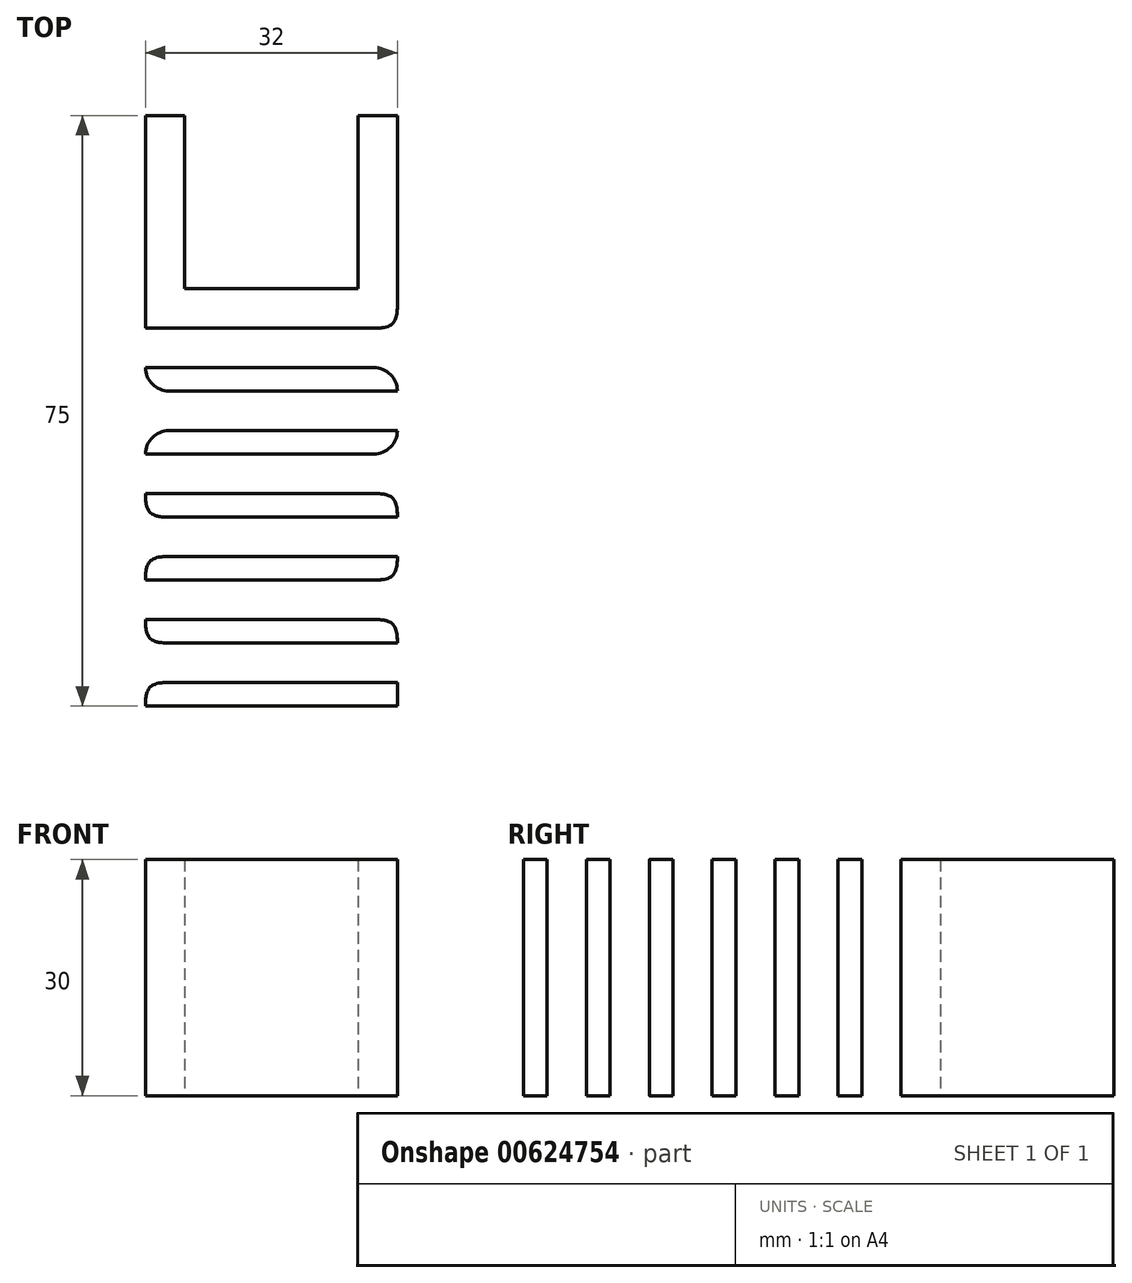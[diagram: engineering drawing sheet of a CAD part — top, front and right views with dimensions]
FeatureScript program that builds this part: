
annotation { "Feature Type Name" : "Feature", "Feature Type Description" : "" }
export const myFeature = defineFeature(function(context is Context, id is Id, definition is map)
    precondition{}
    {
        {
            var Q0;
            Q0=qCreatedBy(makeId("Top.planeOp"),FACE);
            var sketch = newSketch(context, id + "F0", { "sketchPlane" : qUnion([Q0])});
            skLineSegment(sketch, "E0.bottom", {"start": v(-14.17, -5.75) * mm, "end": v(7.83, -5.75) * mm});
            skLineSegment(sketch, "E0.top", {"start": v(-14.17, -27.75) * mm, "end": v(7.83, -27.75) * mm});
            skLineSegment(sketch, "E0.left", {"start": v(-14.17, -5.75) * mm, "end": v(-14.17, -27.75) * mm});
            skLineSegment(sketch, "E0.right", {"start": v(7.83, -5.75) * mm, "end": v(7.83, -27.75) * mm});
            skLineSegment(sketch, "E1.bottom", {"start": v(-14.17, -5.75) * mm, "end": v(-19.17, -5.75) * mm});
            skLineSegment(sketch, "E1.top", {"start": v(-14.17, -27.75) * mm, "end": v(-19.17, -27.75) * mm});
            skLineSegment(sketch, "E1.right", {"start": v(-19.17, -5.75) * mm, "end": v(-19.17, -27.75) * mm});
            skLineSegment(sketch, "E2.bottom", {"start": v(7.83, -5.75) * mm, "end": v(12.83, -5.75) * mm});
            skLineSegment(sketch, "E2.top", {"start": v(7.83, -27.75) * mm, "end": v(12.83, -27.75) * mm});
            skLineSegment(sketch, "E2.right", {"start": v(12.83, -5.75) * mm, "end": v(12.83, -27.75) * mm});
            skLineSegment(sketch, "E3.bottom", {"start": v(-19.17, -27.75) * mm, "end": v(12.83, -27.75) * mm});
            skLineSegment(sketch, "E3.top", {"start": v(-19.17, -32.75) * mm, "end": v(12.83, -32.75) * mm});
            skLineSegment(sketch, "E3.left", {"start": v(-19.17, -27.75) * mm, "end": v(-19.17, -32.75) * mm});
            skLineSegment(sketch, "E3.right", {"start": v(12.83, -27.75) * mm, "end": v(12.83, -32.75) * mm});
            skLineSegment(sketch, "E4.bottom", {"start": v(-19.17, -32.75) * mm, "end": v(-16.17, -32.75) * mm});
            skLineSegment(sketch, "E4.top", {"start": v(-19.17, -37.75) * mm, "end": v(-16.17, -37.75) * mm});
            skLineSegment(sketch, "E4.left", {"start": v(-19.17, -32.75) * mm, "end": v(-19.17, -37.75) * mm});
            skLineSegment(sketch, "E4.right", {"start": v(-16.17, -32.75) * mm, "end": v(-16.17, -37.75) * mm});
            skLineSegment(sketch, "E5.bottom", {"start": v(-19.17, -37.75) * mm, "end": v(9.83, -37.75) * mm});
            skLineSegment(sketch, "E5.top", {"start": v(-16.17, -40.75) * mm, "end": v(12.83, -40.75) * mm});
            skLineSegment(sketch, "E5.left", {"start": v(-19.17, -37.75) * mm, "end": v(-19.17, -37.75) * mm});
            skLineSegment(sketch, "E5.right", {"start": v(12.83, -40.75) * mm, "end": v(12.83, -40.75) * mm});
            skLineSegment(sketch, "E6.bottom", {"start": v(12.83, -40.75) * mm, "end": v(9.83, -40.75) * mm});
            skLineSegment(sketch, "E6.top", {"start": v(12.83, -45.75) * mm, "end": v(9.83, -45.75) * mm});
            skLineSegment(sketch, "E6.left", {"start": v(12.83, -40.75) * mm, "end": v(12.83, -45.75) * mm});
            skLineSegment(sketch, "E6.right", {"start": v(9.83, -40.75) * mm, "end": v(9.83, -45.75) * mm});
            skLineSegment(sketch, "E7.bottom", {"start": v(12.83, -45.75) * mm, "end": v(-16.17, -45.75) * mm});
            skLineSegment(sketch, "E7.top", {"start": v(9.83, -48.75) * mm, "end": v(-19.17, -48.75) * mm});
            skLineSegment(sketch, "E7.left", {"start": v(12.83, -45.75) * mm, "end": v(12.83, -45.75) * mm});
            skLineSegment(sketch, "E7.right", {"start": v(-19.17, -48.75) * mm, "end": v(-19.17, -48.75) * mm});
            skLineSegment(sketch, "E8.bottom", {"start": v(-19.17, -48.75) * mm, "end": v(-16.17, -48.75) * mm});
            skLineSegment(sketch, "E8.top", {"start": v(-19.17, -53.75) * mm, "end": v(-16.17, -53.75) * mm});
            skLineSegment(sketch, "E8.left", {"start": v(-19.17, -48.75) * mm, "end": v(-19.17, -53.75) * mm});
            skLineSegment(sketch, "E8.right", {"start": v(-16.17, -48.75) * mm, "end": v(-16.17, -53.75) * mm});
            skLineSegment(sketch, "E9.bottom", {"start": v(-19.17, -53.75) * mm, "end": v(12.83, -53.75) * mm});
            skLineSegment(sketch, "E9.top", {"start": v(-19.17, -56.75) * mm, "end": v(12.83, -56.75) * mm});
            skLineSegment(sketch, "E9.left", {"start": v(-19.17, -53.75) * mm, "end": v(-19.17, -56.75) * mm});
            skLineSegment(sketch, "E9.right", {"start": v(12.83, -53.75) * mm, "end": v(12.83, -56.75) * mm});
            skPoint(sketch, "E10.visualSharp", {"position": v(12.83, -37.75) * mm});
            skArc(sketch, "E10.filletArc", {"start": v(12.83, -40.75) * mm, "mid": v(11.96, -38.63) * mm, "end": v(9.83, -37.75) * mm});
            skPoint(sketch, "E11.visualSharp", {"position": v(12.83, -48.75) * mm});
            skArc(sketch, "E11.filletArc", {"start": v(9.83, -48.75) * mm, "mid": v(11.96, -47.87) * mm, "end": v(12.83, -45.75) * mm});
            skPoint(sketch, "E12.visualSharp", {"position": v(-19.17, -45.75) * mm});
            skArc(sketch, "E12.filletArc", {"start": v(-16.17, -45.75) * mm, "mid": v(-18.29, -46.63) * mm, "end": v(-19.17, -48.75) * mm});
            skPoint(sketch, "E13.visualSharp", {"position": v(-19.17, -40.75) * mm});
            skArc(sketch, "E13.filletArc", {"start": v(-19.17, -37.75) * mm, "mid": v(-18.29, -39.87) * mm, "end": v(-16.17, -40.75) * mm});
            skLineSegment(sketch, "E14.bottom", {"start": v(12.83, -56.75) * mm, "end": v(9.98, -56.75) * mm});
            skLineSegment(sketch, "E14.top", {"start": v(12.83, -61.75) * mm, "end": v(9.98, -61.75) * mm});
            skLineSegment(sketch, "E14.left", {"start": v(12.83, -56.75) * mm, "end": v(12.83, -61.75) * mm});
            skLineSegment(sketch, "E14.right", {"start": v(9.98, -56.75) * mm, "end": v(9.98, -61.75) * mm});
            skLineSegment(sketch, "E15.bottom", {"start": v(12.83, -61.75) * mm, "end": v(-19.17, -61.75) * mm});
            skLineSegment(sketch, "E15.top", {"start": v(12.83, -64.75) * mm, "end": v(-19.17, -64.75) * mm});
            skLineSegment(sketch, "E15.left", {"start": v(12.83, -61.75) * mm, "end": v(12.83, -64.75) * mm});
            skLineSegment(sketch, "E15.right", {"start": v(-19.17, -61.75) * mm, "end": v(-19.17, -64.75) * mm});
            skLineSegment(sketch, "E16.bottom", {"start": v(-19.17, -64.75) * mm, "end": v(-16.17, -64.75) * mm});
            skLineSegment(sketch, "E16.top", {"start": v(-19.17, -69.75) * mm, "end": v(-16.17, -69.75) * mm});
            skLineSegment(sketch, "E16.left", {"start": v(-19.17, -64.75) * mm, "end": v(-19.17, -69.75) * mm});
            skLineSegment(sketch, "E16.right", {"start": v(-16.17, -64.75) * mm, "end": v(-16.17, -69.75) * mm});
            skLineSegment(sketch, "E17.bottom", {"start": v(-19.17, -69.75) * mm, "end": v(12.83, -69.75) * mm});
            skLineSegment(sketch, "E17.top", {"start": v(-19.17, -72.75) * mm, "end": v(12.83, -72.75) * mm});
            skLineSegment(sketch, "E17.left", {"start": v(-19.17, -69.75) * mm, "end": v(-19.17, -72.75) * mm});
            skLineSegment(sketch, "E17.right", {"start": v(12.83, -69.75) * mm, "end": v(12.83, -72.75) * mm});
            skLineSegment(sketch, "E18.bottom", {"start": v(12.83, -72.75) * mm, "end": v(9.98, -72.75) * mm});
            skLineSegment(sketch, "E18.top", {"start": v(12.83, -77.75) * mm, "end": v(9.98, -77.75) * mm});
            skLineSegment(sketch, "E18.left", {"start": v(12.83, -72.75) * mm, "end": v(12.83, -77.75) * mm});
            skLineSegment(sketch, "E18.right", {"start": v(9.98, -72.75) * mm, "end": v(9.98, -77.75) * mm});
            skLineSegment(sketch, "E19.bottom", {"start": v(12.83, -77.75) * mm, "end": v(-19.17, -77.75) * mm});
            skLineSegment(sketch, "E19.top", {"start": v(12.83, -80.75) * mm, "end": v(-19.17, -80.75) * mm});
            skLineSegment(sketch, "E19.left", {"start": v(12.83, -77.75) * mm, "end": v(12.83, -80.75) * mm});
            skLineSegment(sketch, "E19.right", {"start": v(-19.17, -77.75) * mm, "end": v(-19.17, -80.75) * mm});
            skSolve(sketch);
        }
        {
            var Q0;
            Q0=makeQuery(id+"F0.imprint","IMPRINT",FACE,{"disambiguationData":[TD([[makeQuery(id+"F0.imprint","IMPRINT",EDGE,{"derivedFrom":sQuery(id+"F0.wireOp",EDGE,"E1.bottom")}),1.0]])]});
            var Q1;
            Q1=makeQuery(id+"F0.imprint","IMPRINT",FACE,{"disambiguationData":[TD([[makeQuery(id+"F0.imprint","IMPRINT",EDGE,{"derivedFrom":sQuery(id+"F0.wireOp",EDGE,"E3.top")}),1.0]])]});
            var Q2;
            Q2=makeQuery(id+"F0.imprint","IMPRINT",FACE,{"disambiguationData":[TD([[makeQuery(id+"F0.imprint","IMPRINT",EDGE,{"derivedFrom":sQuery(id+"F0.wireOp",EDGE,"E2.bottom")}),-1.0]])]});
            var Q3;
            Q3=makeQuery(id+"F0.imprint","IMPRINT",FACE,{"disambiguationData":[TD([[makeQuery(id+"F0.imprint","IMPRINT",EDGE,{"derivedFrom":sQuery(id+"F0.wireOp",EDGE,"E4.bottom")}),-1.0]])]});
            var Q4;
            Q4=makeQuery(id+"F0.imprint","IMPRINT",FACE,{"disambiguationData":[TD([[makeQuery(id+"F0.imprint","IMPRINT",EDGE,{"derivedFrom":sQuery(id+"F0.wireOp",EDGE,"E5.top")}),1.0]])]});
            var Q5;
            Q5=makeQuery(id+"F0.imprint","IMPRINT",FACE,{"disambiguationData":[TD([[makeQuery(id+"F0.imprint","IMPRINT",EDGE,{"derivedFrom":sQuery(id+"F0.wireOp",EDGE,"E6.bottom")}),1.0]])]});
            var Q6;
            Q6=makeQuery(id+"F0.imprint","IMPRINT",FACE,{"disambiguationData":[TD([[makeQuery(id+"F0.imprint","IMPRINT",EDGE,{"derivedFrom":sQuery(id+"F0.wireOp",EDGE,"E7.top")}),-1.0]])]});
            var Q7;
            Q7=makeQuery(id+"F0.imprint","IMPRINT",FACE,{"disambiguationData":[TD([[makeQuery(id+"F0.imprint","IMPRINT",EDGE,{"derivedFrom":sQuery(id+"F0.wireOp",EDGE,"E8.bottom")}),-1.0]])]});
            var Q8;
            Q8=makeQuery(id+"F0.imprint","IMPRINT",FACE,{"disambiguationData":[TD([[makeQuery(id+"F0.imprint","IMPRINT",EDGE,{"derivedFrom":sQuery(id+"F0.wireOp",EDGE,"E9.top")}),1.0]])]});
            var Q9;
            Q9=makeQuery(id+"F0.imprint","IMPRINT",FACE,{"disambiguationData":[TD([[makeQuery(id+"F0.imprint","IMPRINT",EDGE,{"derivedFrom":sQuery(id+"F0.wireOp",EDGE,"E14.bottom")}),1.0]])]});
            var Q10;
            Q10=makeQuery(id+"F0.imprint","IMPRINT",FACE,{"disambiguationData":[TD([[makeQuery(id+"F0.imprint","IMPRINT",EDGE,{"derivedFrom":sQuery(id+"F0.wireOp",EDGE,"E15.top")}),-1.0]])]});
            var Q11;
            Q11=makeQuery(id+"F0.imprint","IMPRINT",FACE,{"disambiguationData":[TD([[makeQuery(id+"F0.imprint","IMPRINT",EDGE,{"derivedFrom":sQuery(id+"F0.wireOp",EDGE,"E16.bottom")}),-1.0]])]});
            var Q12;
            Q12=makeQuery(id+"F0.imprint","IMPRINT",FACE,{"disambiguationData":[TD([[makeQuery(id+"F0.imprint","IMPRINT",EDGE,{"derivedFrom":sQuery(id+"F0.wireOp",EDGE,"E17.top")}),1.0]])]});
            var Q13;
            Q13=makeQuery(id+"F0.imprint","IMPRINT",FACE,{"disambiguationData":[TD([[makeQuery(id+"F0.imprint","IMPRINT",EDGE,{"derivedFrom":sQuery(id+"F0.wireOp",EDGE,"E18.bottom")}),1.0]])]});
            var Q14;
            Q14=makeQuery(id+"F0.imprint","IMPRINT",FACE,{"disambiguationData":[TD([[makeQuery(id+"F0.imprint","IMPRINT",EDGE,{"derivedFrom":sQuery(id+"F0.wireOp",EDGE,"E19.top")}),-1.0]])]});
            extrude(context, id + "F1", {"entities" : qUnion([Q0, Q1, Q2, Q3, Q4, Q5, Q6, Q7, Q8, Q9, Q10, Q11, Q12, Q13, Q14]), "depth" : 30 * mm, "offsetDistance" : 25 * mm});
        }
        {
            var Q0;
            Q0=makeQuery(id+"F1.opExtrude","SWEPT_EDGE",EDGE,{"disambiguationData":[OSD([sQuery(id+"F0.wireOp",EDGE,"E4.right"),sQuery(id+"F0.wireOp",EDGE,"E5.bottom")])]});
            var Q1;
            Q1=makeQuery(id+"F1.opExtrude","SWEPT_EDGE",EDGE,{"disambiguationData":[OSD([sQuery(id+"F0.wireOp",EDGE,"E3.top"),sQuery(id+"F0.wireOp",EDGE,"E4.bottom"),sQuery(id+"F0.wireOp",EDGE,"E4.right")])]});
            var Q2;
            Q2=makeQuery(id+"F1.opExtrude","SWEPT_EDGE",EDGE,{"disambiguationData":[OSD([sQuery(id+"F0.wireOp",EDGE,"E5.top"),sQuery(id+"F0.wireOp",EDGE,"E6.bottom"),sQuery(id+"F0.wireOp",EDGE,"E6.right")])]});
            var Q3;
            Q3=makeQuery(id+"F1.opExtrude","SWEPT_EDGE",EDGE,{"disambiguationData":[OSD([sQuery(id+"F0.wireOp",EDGE,"E6.right"),sQuery(id+"F0.wireOp",EDGE,"E7.bottom")])]});
            var Q4;
            Q4=makeQuery(id+"F1.opExtrude","SWEPT_EDGE",EDGE,{"disambiguationData":[OSD([sQuery(id+"F0.wireOp",EDGE,"E7.top"),sQuery(id+"F0.wireOp",EDGE,"E8.bottom"),sQuery(id+"F0.wireOp",EDGE,"E8.right")])]});
            var Q5;
            Q5=makeQuery(id+"F1.opExtrude","SWEPT_EDGE",EDGE,{"disambiguationData":[OSD([sQuery(id+"F0.wireOp",EDGE,"E8.right"),sQuery(id+"F0.wireOp",EDGE,"E9.bottom")])]});
            var Q6;
            Q6=makeQuery(id+"F1.opExtrude","SWEPT_EDGE",EDGE,{"disambiguationData":[OSD([sQuery(id+"F0.wireOp",EDGE,"E9.bottom"),sQuery(id+"F0.wireOp",EDGE,"E9.right")])]});
            var Q7;
            Q7=makeQuery(id+"F1.opExtrude","SWEPT_EDGE",EDGE,{"disambiguationData":[OSD([sQuery(id+"F0.wireOp",EDGE,"E15.top"),sQuery(id+"F0.wireOp",EDGE,"E15.left")])]});
            var Q8;
            Q8=makeQuery(id+"F1.opExtrude","SWEPT_EDGE",EDGE,{"disambiguationData":[OSD([sQuery(id+"F0.wireOp",EDGE,"E17.bottom"),sQuery(id+"F0.wireOp",EDGE,"E17.right")])]});
            var Q9;
            Q9=makeQuery(id+"F1.opExtrude","SWEPT_EDGE",EDGE,{"disambiguationData":[OSD([sQuery(id+"F0.wireOp",EDGE,"E17.top"),sQuery(id+"F0.wireOp",EDGE,"E18.bottom"),sQuery(id+"F0.wireOp",EDGE,"E18.right")])]});
            var Q10;
            Q10=makeQuery(id+"F1.opExtrude","SWEPT_EDGE",EDGE,{"disambiguationData":[OSD([sQuery(id+"F0.wireOp",EDGE,"E18.right"),sQuery(id+"F0.wireOp",EDGE,"E19.bottom")])]});
            var Q11;
            Q11=makeQuery(id+"F1.opExtrude","SWEPT_EDGE",EDGE,{"disambiguationData":[OSD([sQuery(id+"F0.wireOp",EDGE,"E17.top"),sQuery(id+"F0.wireOp",EDGE,"E17.left")])]});
            var Q12;
            Q12=makeQuery(id+"F1.opExtrude","SWEPT_EDGE",EDGE,{"disambiguationData":[OSD([sQuery(id+"F0.wireOp",EDGE,"E15.bottom"),sQuery(id+"F0.wireOp",EDGE,"E15.right")])]});
            var Q13;
            Q13=makeQuery(id+"F1.opExtrude","SWEPT_EDGE",EDGE,{"disambiguationData":[OSD([sQuery(id+"F0.wireOp",EDGE,"E9.top"),sQuery(id+"F0.wireOp",EDGE,"E14.bottom"),sQuery(id+"F0.wireOp",EDGE,"E14.right")])]});
            var Q14;
            Q14=makeQuery(id+"F1.opExtrude","SWEPT_EDGE",EDGE,{"disambiguationData":[OSD([sQuery(id+"F0.wireOp",EDGE,"E14.right"),sQuery(id+"F0.wireOp",EDGE,"E15.bottom")])]});
            var Q15;
            Q15=makeQuery(id+"F1.opExtrude","SWEPT_EDGE",EDGE,{"disambiguationData":[OSD([sQuery(id+"F0.wireOp",EDGE,"E9.top"),sQuery(id+"F0.wireOp",EDGE,"E9.left")])]});
            var Q16;
            Q16=makeQuery(id+"F1.opExtrude","SWEPT_EDGE",EDGE,{"disambiguationData":[OSD([sQuery(id+"F0.wireOp",EDGE,"E15.top"),sQuery(id+"F0.wireOp",EDGE,"E16.bottom"),sQuery(id+"F0.wireOp",EDGE,"E16.right")])]});
            var Q17;
            Q17=makeQuery(id+"F1.opExtrude","SWEPT_EDGE",EDGE,{"disambiguationData":[OSD([sQuery(id+"F0.wireOp",EDGE,"E16.right"),sQuery(id+"F0.wireOp",EDGE,"E17.bottom")])]});
            fillet(context, id + "F2", {"entities" : qUnion([Q0, Q1, Q2, Q3, Q4, Q5, Q6, Q7, Q8, Q9, Q10, Q11, Q12, Q13, Q14, Q15, Q16, Q17]), "radius" : 3 * mm, "tangentPropagation" : true, "rho" : .6, "crossSection" : FilletCrossSection.CONIC, "allowEdgeOverflow" : false});
        }
    });
